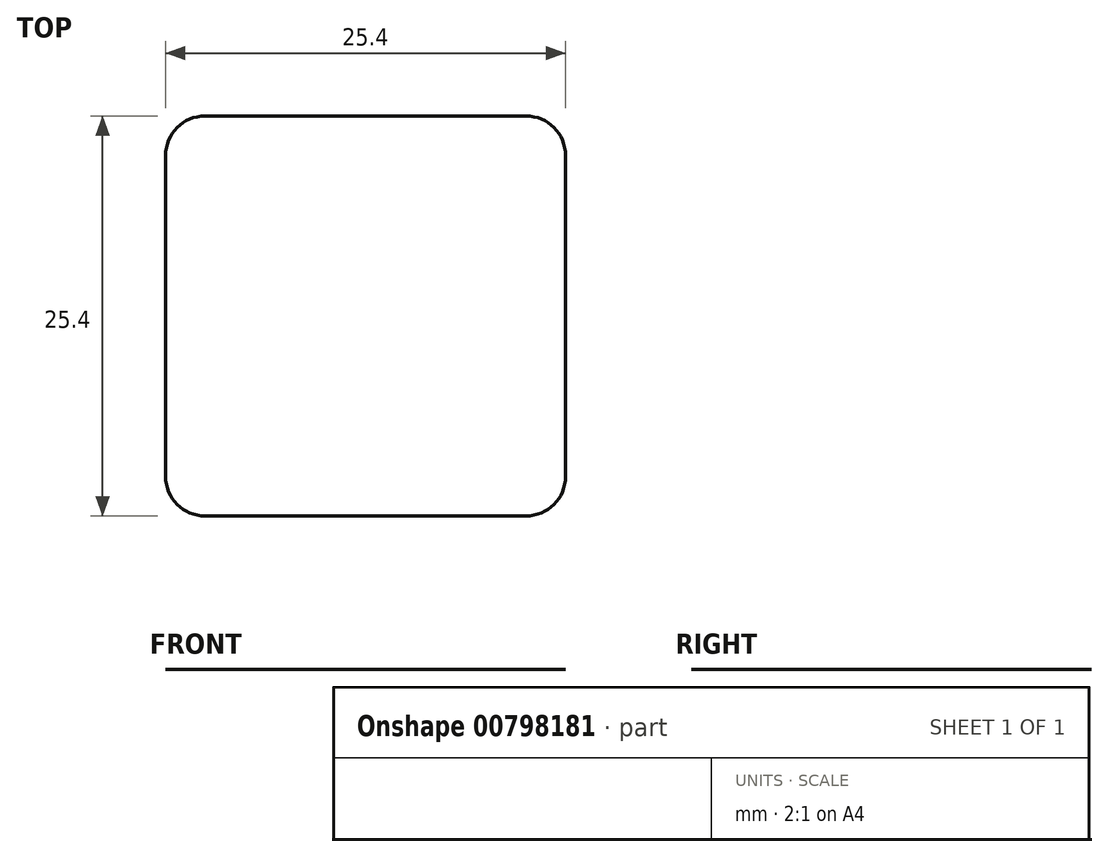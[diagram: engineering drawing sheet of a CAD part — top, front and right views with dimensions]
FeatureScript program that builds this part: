
annotation { "Feature Type Name" : "Feature", "Feature Type Description" : "" }
export const myFeature = defineFeature(function(context is Context, id is Id, definition is map)
    precondition{}
    {
        {
            var Q0;
            Q0=qCreatedBy(makeId("Top.planeOp"),FACE);
            var sketch = newSketch(context, id + "F0", { "sketchPlane" : qUnion([Q0])});
            skLineSegment(sketch, "E0.bottom", {"start": v(12.7, -12.7) * mm, "end": v(-12.7, -12.7) * mm});
            skLineSegment(sketch, "E0.top", {"start": v(12.7, 12.7) * mm, "end": v(-12.7, 12.7) * mm});
            skLineSegment(sketch, "E0.left", {"start": v(12.7, -12.7) * mm, "end": v(12.7, 12.7) * mm});
            skLineSegment(sketch, "E0.right", {"start": v(-12.7, -12.7) * mm, "end": v(-12.7, 12.7) * mm});
            skPoint(sketch, "E0.middle", {"position": v(0, 0) * mm});
            skSolve(sketch);
        }
        {
            var Q0;
            Q0 = qSketchRegion(id + "F0", true);
            extrude(context, id + "F1", {"entities" : qUnion([Q0]), "depth" : 1 / 203.2 * mm, "offsetDistance" : 25 * mm});
        }
        {
            var Q0;
            Q0=makeQuery(id+"F1.opExtrude","SWEPT_EDGE",EDGE,{"disambiguationData":[OSD([sQuery(id+"F0.wireOp",EDGE,"E0.bottom"),sQuery(id+"F0.wireOp",EDGE,"E0.left")])]});
            var Q1;
            Q1=makeQuery(id+"F1.opExtrude","SWEPT_EDGE",EDGE,{"disambiguationData":[OSD([sQuery(id+"F0.wireOp",EDGE,"E0.bottom"),sQuery(id+"F0.wireOp",EDGE,"E0.right")])]});
            var Q2;
            Q2=makeQuery(id+"F1.opExtrude","SWEPT_EDGE",EDGE,{"disambiguationData":[OSD([sQuery(id+"F0.wireOp",EDGE,"E0.top"),sQuery(id+"F0.wireOp",EDGE,"E0.left")])]});
            var Q3;
            Q3=makeQuery(id+"F1.opExtrude","SWEPT_EDGE",EDGE,{"disambiguationData":[OSD([sQuery(id+"F0.wireOp",EDGE,"E0.top"),sQuery(id+"F0.wireOp",EDGE,"E0.right")])]});
            fillet(context, id + "F2", {"entities" : qUnion([Q0, Q1, Q2, Q3]), "radius" : 2.5 * mm, "tangentPropagation" : true, "allowEdgeOverflow" : false});
        }
    });
